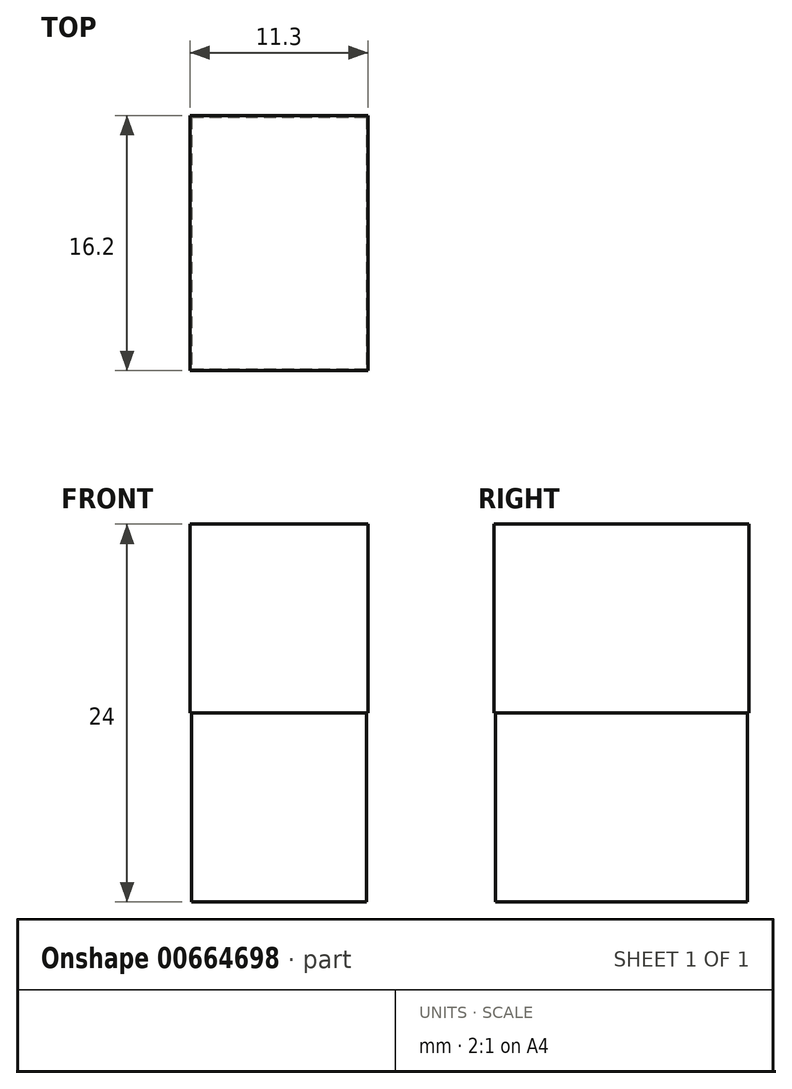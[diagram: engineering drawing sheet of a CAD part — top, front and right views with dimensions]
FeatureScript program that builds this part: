
annotation { "Feature Type Name" : "Feature", "Feature Type Description" : "" }
export const myFeature = defineFeature(function(context is Context, id is Id, definition is map)
    precondition{}
    {
        {
            var Q0;
            Q0=qCreatedBy(makeId("Top.planeOp"),FACE);
            var sketch = newSketch(context, id + "F0", { "sketchPlane" : qUnion([Q0])});
            skLineSegment(sketch, "E0.bottom", {"start": v(0, 0) * mm, "end": v(11.1, 0) * mm});
            skLineSegment(sketch, "E0.top", {"start": v(0, -16) * mm, "end": v(11.1, -16) * mm});
            skLineSegment(sketch, "E0.left", {"start": v(0, 0) * mm, "end": v(0, -16) * mm});
            skLineSegment(sketch, "E0.right", {"start": v(11.1, 0) * mm, "end": v(11.1, -16) * mm});
            skSolve(sketch);
        }
        {
            var Q0;
            Q0 = qSketchRegion(id + "F0", true);
            extrude(context, id + "F1", {"entities" : qUnion([Q0]), "depth" : 12 * mm, "offsetDistance" : 25 * mm});
        }
        {
            var Q0;
            Q0=makeQuery(id+"F1.opExtrude","CAP_FACE",FACE,{"disambiguationData":[OSD([sQuery(id+"F0.wireOp",EDGE,"E0.bottom"),sQuery(id+"F0.wireOp",EDGE,"E0.top"),sQuery(id+"F0.wireOp",EDGE,"E0.left"),sQuery(id+"F0.wireOp",EDGE,"E0.right")])],"isStart":false});
            var sketch = newSketch(context, id + "F2", { "sketchPlane" : qUnion([Q0])});
            skLineSegment(sketch, "E1.bottom", {"start": v(11.2, -16.1) * mm, "end": v(-0.1, -16.1) * mm});
            skLineSegment(sketch, "E1.top", {"start": v(11.2, 0.1) * mm, "end": v(-0.1, 0.1) * mm});
            skLineSegment(sketch, "E1.left", {"start": v(11.2, -16.1) * mm, "end": v(11.2, 0.1) * mm});
            skLineSegment(sketch, "E1.right", {"start": v(-0.1, -16.1) * mm, "end": v(-0.1, 0.1) * mm});
            skPoint(sketch, "E1.middle", {"position": v(5.55, -8) * mm});
            skPoint(sketch, "E1.middle.positionSnap0", {"position": v(0, -8) * mm});
            skPoint(sketch, "E1.middle.positionSnap1", {"position": v(5.55, -16) * mm});
            skPoint(sketch, "E1.centerSnap0", {"position": v(0, -8) * mm});
            skPoint(sketch, "E1.centerSnap1", {"position": v(5.55, -16) * mm});
            skSolve(sketch);
        }
        {
            var Q0;
            Q0 = qSketchRegion(id + "F2", true);
            extrude(context, id + "F3", {"entities" : qUnion([Q0]), "operationType" : NewBodyOperationType.ADD, "depth" : 12 * mm, "offsetDistance" : 25 * mm});
        }
    });
